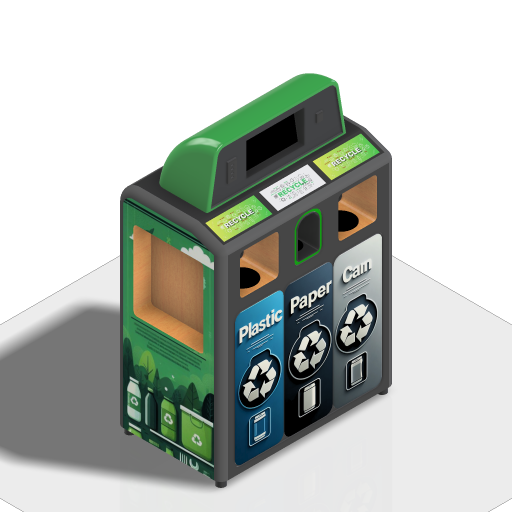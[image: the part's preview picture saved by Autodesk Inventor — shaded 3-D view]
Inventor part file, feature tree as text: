
AUTODESK INVENTOR PART (.ipt)
format: ipt  version: 2024.1 (Build 281209000, 209)  size: 2,275,328 bytes
history: native  units: mm
features: projected_geometry x24, sketch x20, extrude x16, other x16, plane x6, fillet x5, chamfer x1
ambient origin geometry x8: Origin, YZ Plane, XZ Plane, XY Plane, X Axis, Y Axis, Z Axis, Center Point
bodies: Solid1 (feature_tree)
feature tree (88):
  extrude  "Extrusion1"  Depth=40.0mm
  chamfer  "Chamfer1"  Distance=1200.0mm
  fillet  "Fillet1"  Radius=40.0mm
  extrude  "Extrusion2"  Depth=20.0mm
  extrude  "Extrusion3"  Depth=60.0mm
  extrude  "Extrusion4"  Depth=450.0mm
  fillet  "Fillet2"  Radius=100.0mm
  extrude  "Extrusion5"  Depth=200.0mm
  extrude  "Extrusion6"  Depth=50.0mm
  extrude  "Extrusion7"  Depth=10.0mm TaperAngle=0.0deg
  extrude  "Extrusion8"  Depth=2.5mm
  extrude  "Extrusion12"  Depth=2.5mm
  fillet  "Fillet3"  Radius=2.5mm
  fillet  "Fillet4"  Radius=5.0mm
  extrude  "Extrusion10"  Depth=40.0mm
  extrude  "Extrusion11"  Depth=40.0mm
  fillet  "Fillet5"  Radius=40.0mm
  extrude  "Extrusion13"  Depth=5.0mm
  extrude  "Extrusion14"  Depth=10.0mm TaperAngle=0.0deg
  extrude  "Extrusion15"  Depth=300.0mm TaperAngle=0.0deg
  plane  "Work Plane1"
  sketch  "Sketch18"  dims[d47=0.0mm d48=0.0mm d52=60.0mm]
  other  "Decal2"
  other  "Decal3"
  other  "Decal4"
  plane  "Work Plane2"
  plane  "Work Plane3"
  plane  "Work Plane4"
  other  "Decal7"
  other  "Decal8"
  plane  "Work Plane5"
  extrude  "Extrusion16"  Depth=60.0mm
  plane  "Work Plane6"
  sketch  "Sketch26"  dims[d61=80.0mm]
  other  "Decal10"
  other  "Decal11"
  other  "Decal12"
  extrude  "Extrusion17"  Depth=10.0mm TaperAngle=0.0deg
  sketch  "Sketch1"  dims[d0=600.0mm d1=1000.0mm d2=1200.0mm d3=0.0mm d5=40.0mm]
  sketch  "Sketch3"  dims[d6=60.0mm d7=2.0mm d8=12.217305mm d9=20.0mm]
  projected_geometry  "Projected Loop1"
  sketch  "Sketch4"  dims[d10=60.0mm d11=60.0mm]
  projected_geometry  "Projected Loop2"
  sketch  "Sketch5"  dims[d12=120.0mm d13=450.0mm d14=100.0mm d15=0.0mm]
  projected_geometry  "Projected Loop3"
  sketch  "Sketch6"  dims[d16=150.0mm d17=200.0mm]
  projected_geometry  "Projected Loop4"
  sketch  "Sketch7"  dims[d18=120.0mm d19=50.0mm]
  projected_geometry  "Projected Loop5"
  sketch  "Sketch8"  dims[d20=10.0mm d21=200.0mm d22=0.0mm]
  projected_geometry  "Projected Loop6"
  sketch  "Sketch9"  dims[d23=800.0mm d26=2.5mm]
  projected_geometry  "Projected Loop7"
  sketch  "Sketch11"  dims[d27=2.5mm d28=2.5mm d29=2.5mm d30=5.0mm]
  projected_geometry  "Projected Loop9"
  sketch  "Sketch12"  dims[d31=5.0mm d32=0.0mm d33=40.0mm]
  projected_geometry  "Projected Loop10"
  sketch  "Sketch13"  dims[d34=280.0mm d35=5.0mm d36=40.0mm]
  projected_geometry  "Projected Loop11"
  projected_geometry  "Projected Loop12"
  projected_geometry  "Projected Loop13"
  sketch  "Sketch14"  dims[d37=20.0mm d38=5.0mm]
  projected_geometry  "Projected Loop15"
  sketch  "Sketch15"  dims[d39=5.0mm d40=0.0mm d41=10.0mm d42=0.0mm]
  projected_geometry  "Projected Loop16"
  projected_geometry  "Projected Loop17"
  sketch  "Sketch16"  dims[d43=800.0mm d45=300.0mm d46=0.0mm]
  projected_geometry  "Projected Loop18"
  projected_geometry  "Projected Loop19"
  projected_geometry  "Projected Loop20"
  projected_geometry  "Projected Loop21"
  projected_geometry  "Projected Loop22"
  other  "Image1"
  other  "Image2"
  other  "Image3"
  sketch  "Sketch21"  dims[d53=10.0mm d55=332.0mm d56=0.0mm]
  projected_geometry  "Projected Loop24"
  other  "Image6"
  sketch  "Sketch22"  dims[d59=50.0mm]
  other  "Image7"
  projected_geometry  "Projected Loop25"
  sketch  "Sketch25"  dims[d60=190.0mm]
  projected_geometry  "Projected Loop26"
  other  "Image10"
  other  "Image12"
  other  "Image13"
  sketch  "Sketch27"  dims[d62=17.453293mm d63=80.0mm d64=6.0mm d65=15.0mm d66=40.0mm d68=20.0mm d69=10.0mm d71=10.0mm d73=20.0mm d74=20.0mm d75=5.0mm d76=60.0mm d77=3.0mm d78=10.0mm d79=0.0mm d80=100.0mm d81=340.0mm d82=50.0mm d84=50.0mm d85=0.0mm d86=0.0mm d87=5.0mm d88=5.0mm d89=5.0mm d90=30.0mm d91=20.0mm d92=260.0mm d93=840.0mm d94=5.0mm d95=30.0mm d96=200.0mm d97=200.0mm d98=35.0mm d99=30.0mm d100=30.0mm d101=30.0mm d102=5.0mm d103=0.0mm d104=20.0mm d105=230.0mm d106=220.0mm d107=200.0mm d108=0.0mm d109=150.0mm d110=10.0mm d111=0.0mm d112=100.0mm d142=755.0mm d159=755.0mm d192=100.0mm d200=309.0mm d215=425.0mm d217=520.0mm d226=520.0mm d243=747.75mm d257=10.0mm d258=10.0mm d259=0.0mm d260=121.0mm d325=115.0mm d338=115.0mm d343=115.0mm d355=50.0mm d356=40.0mm d357=0.0mm d244=0.0mm d245=0.0mm d246=0.0mm]
  projected_geometry  "Projected Loop27"
